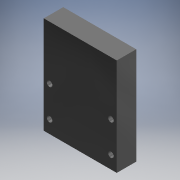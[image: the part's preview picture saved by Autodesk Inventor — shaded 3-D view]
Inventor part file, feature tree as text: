
AUTODESK INVENTOR PART (.ipt)
format: ipt  version: 2019 (Build 230136000, 136)  size: 103,424 bytes
history: native  units: mm (DEFAULTED — no unit token found)
features: extrude x2, sketch x2, plane x1, mirror x1
ambient origin geometry x8: Origin, YZ Plane, XZ Plane, XY Plane, X Axis, Y Axis, Z Axis, Center Point
bodies: Solid1 (feature_tree)
feature tree (6):
  extrude  "Extrusion1"  Depth=50.8mm
  extrude  "Extrusion2"  Depth=10.16mm
  plane  "Work Plane1"
  mirror  "Mirror1"
  sketch  "Sketch1"  dims[d0=38.1mm d1=50.8mm]
  sketch  "Sketch2"  dims[d2=10.16mm d3=0.0mm d4=3.048mm d5=3.048mm d6=16.002mm d7=6.731mm d8=2.921mm d9=2.921mm d10=6.35mm d11=0.0mm]
